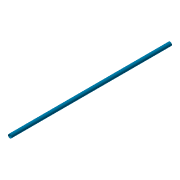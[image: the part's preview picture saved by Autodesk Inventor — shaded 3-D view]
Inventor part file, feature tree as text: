
AUTODESK INVENTOR PART (.ipt)
format: ipt  version: 2016 (Build 200138000, 138)  size: 99,840 bytes
history: native  units: in
note: dims shown in document units (in); Inventor stores cm internally (conversion verified against a paired STEP export)
features: sketch x4, extrude x2, plane x2, hole x1, other x1
ambient origin geometry x8: Origin, YZ Plane, XZ Plane, XY Plane, X Axis, Y Axis, Z Axis, Center Point
bodies: Solid1 (feature_tree)
feature tree (10):
  extrude  "Extrusion1"  Depth=0.1417in
  sketch  "Sketch4"  dims[d3=107.0866in d4=0.0in d16=0.7874in]
  plane  "Work Plane2"
  hole  "Hole2"  [1 undecoded]
  other  "Work Point1"
  plane  "Work Plane3"
  extrude  "Extrusion2"  Depth=1.1811in
  sketch  "Sketch1"  dims[d0=2.4803in d2=0.1417in]
  sketch  "Sketch5"  dims[d18=0.1772in d19=0.75in d20=0.375in d21=0.25in d22=0.5635in d23=1.0in d24=0.8108in d25=1.1811in]
  sketch  "Sketch6"  dims[d26=1.0in d27=0.0in d28=0.0in d29=0.3265in]
note: 1 required parameter value undecoded (feature->parameter linkage not recoverable at this tier; creation-order binding heuristic only, values carry confidence <= 0.55)
